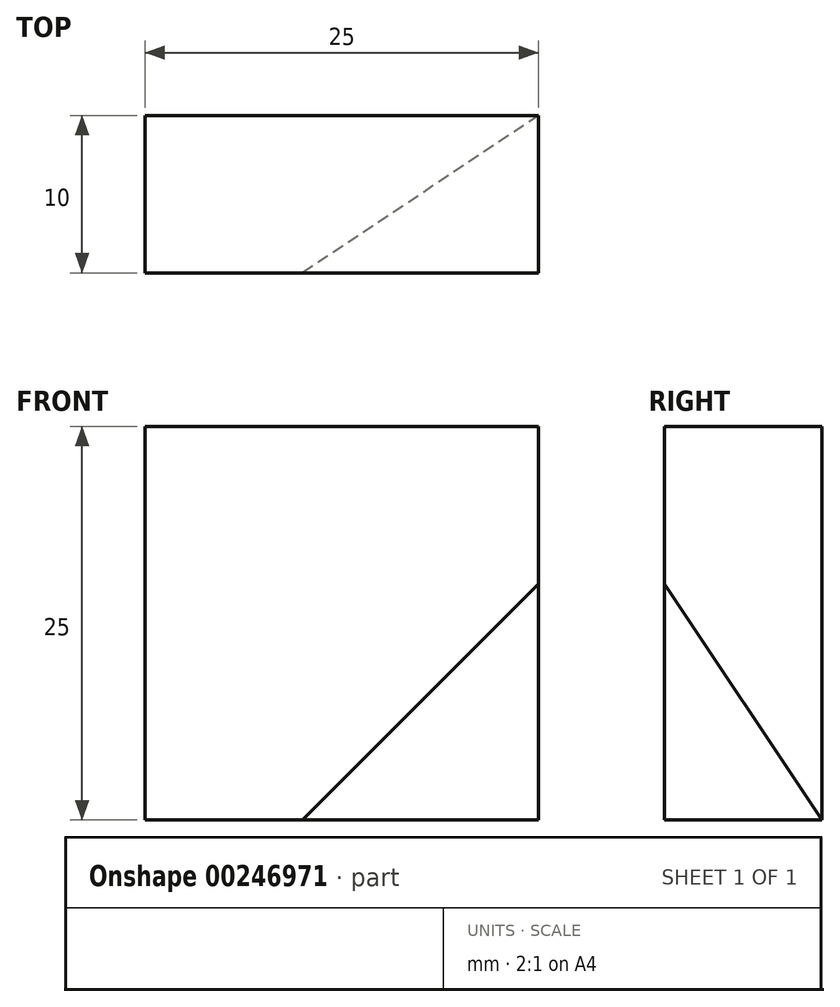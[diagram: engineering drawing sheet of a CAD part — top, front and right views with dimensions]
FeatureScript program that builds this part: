
annotation { "Feature Type Name" : "Feature", "Feature Type Description" : "" }
export const myFeature = defineFeature(function(context is Context, id is Id, definition is map)
    precondition{}
    {
        {
            var Q0;
            Q0=qCreatedBy(makeId("Front.planeOp"),FACE);
            var sketch = newSketch(context, id + "F0", { "sketchPlane" : qUnion([Q0])});
            skLineSegment(sketch, "E0.bottom", {"start": v(0, 0) * mm, "end": v(25, 0) * mm});
            skLineSegment(sketch, "E0.top", {"start": v(0, 25) * mm, "end": v(25, 25) * mm});
            skLineSegment(sketch, "E0.left", {"start": v(0, 0) * mm, "end": v(0, 25) * mm});
            skLineSegment(sketch, "E0.right", {"start": v(25, 0) * mm, "end": v(25, 25) * mm});
            skLineSegment(sketch, "E1", {"start": v(25, 0) * mm, "end": v(25, 15) * mm});
            skLineSegment(sketch, "E2", {"start": v(25, 15) * mm, "end": v(10, 0) * mm});
            skLineSegment(sketch, "E3", {"start": v(10, 0) * mm, "end": v(25, 0) * mm});
            skSolve(sketch);
        }
        {
            var Q0;
            Q0 = qSketchRegion(id + "F0", true);
            extrude(context, id + "F1", {"entities" : qUnion([Q0]), "depth" : 10 * mm});
        }
        {
            var Q0;
            Q0=makeQuery(id+"F1.opExtrude","SWEPT_FACE",FACE,{"disambiguationData":[OSD([sQuery(id+"F0.wireOp",EDGE,"E0.bottom"),sQuery(id+"F0.wireOp",EDGE,"E3")])]});
            var sketch = newSketch(context, id + "F2", { "sketchPlane" : qUnion([Q0])});
            skLineSegment(sketch, "E4", {"start": v(25, 10) * mm, "end": v(10, 10) * mm});
            skLineSegment(sketch, "E5", {"start": v(25, 10) * mm, "end": v(25, 0) * mm});
            skLineSegment(sketch, "E6", {"start": v(25, 0) * mm, "end": v(10, 10) * mm});
            skSolve(sketch);
        }
        {
            var Q0;
            Q0=makeQuery(id+"F1.opExtrude","CAP_FACE",FACE,{"disambiguationData":[OSD([sQuery(id+"F0.wireOp",EDGE,"E0.bottom"),sQuery(id+"F0.wireOp",EDGE,"E0.top"),sQuery(id+"F0.wireOp",EDGE,"E0.left"),sQuery(id+"F0.wireOp",EDGE,"E0.right"),sQuery(id+"F0.wireOp",EDGE,"E1"),sQuery(id+"F0.wireOp",EDGE,"E3")])],"isStart":false});
            var sketch = newSketch(context, id + "F3", { "sketchPlane" : qUnion([Q0])});
            skLineSegment(sketch, "E7", {"start": v(25, 0) * mm, "end": v(25, 15) * mm});
            skLineSegment(sketch, "E8", {"start": v(25, 0) * mm, "end": v(10, 0) * mm});
            skLineSegment(sketch, "E9", {"start": v(10, 0) * mm, "end": v(25, 15) * mm});
            skSolve(sketch);
        }
        {
            var Q0;
            Q0=sQuery(id+"F3.wireOp",VERTEX,"E9.end");
            var Q1;
            Q1=sQuery(id+"F3.wireOp",VERTEX,"E9.start");
            var Q2;
            Q2=sQuery(id+"F2.wireOp",VERTEX,"E6.start");
            cPlane(context, id + "F4", {"entities" : qUnion([Q0, Q1, Q2]), "cplaneType" : CPlaneType.THREE_POINT, "offset" : 25 * mm, "width" : 150 * mm, "height" : 150 * mm});
        }
        {
            var Q0;
            Q0=qCreatedBy(id+"F4.planeOp",FACE);
            var sketch = newSketch(context, id + "F5", { "sketchPlane" : qUnion([Q0])});
            skCircle(sketch, "E10", {"center": v(-17.75, 4.15) * mm, "radius": 14.92 * mm});
            skSolve(sketch);
        }
        {
            var Q0;
            Q0=makeQuery(id+"F5.imprint","IMPRINT",FACE,{"disambiguationData":[TD([[makeQuery(id+"F5.imprint","IMPRINT",EDGE,{"derivedFrom":sQuery(id+"F5.wireOp",EDGE,"E10")}),1.0]])]});
            extrude(context, id + "F6", {"entities" : qUnion([Q0]), "operationType" : NewBodyOperationType.REMOVE, "oppositeDirection" : true, "depth" : 16.2 * mm});
        }
    });
